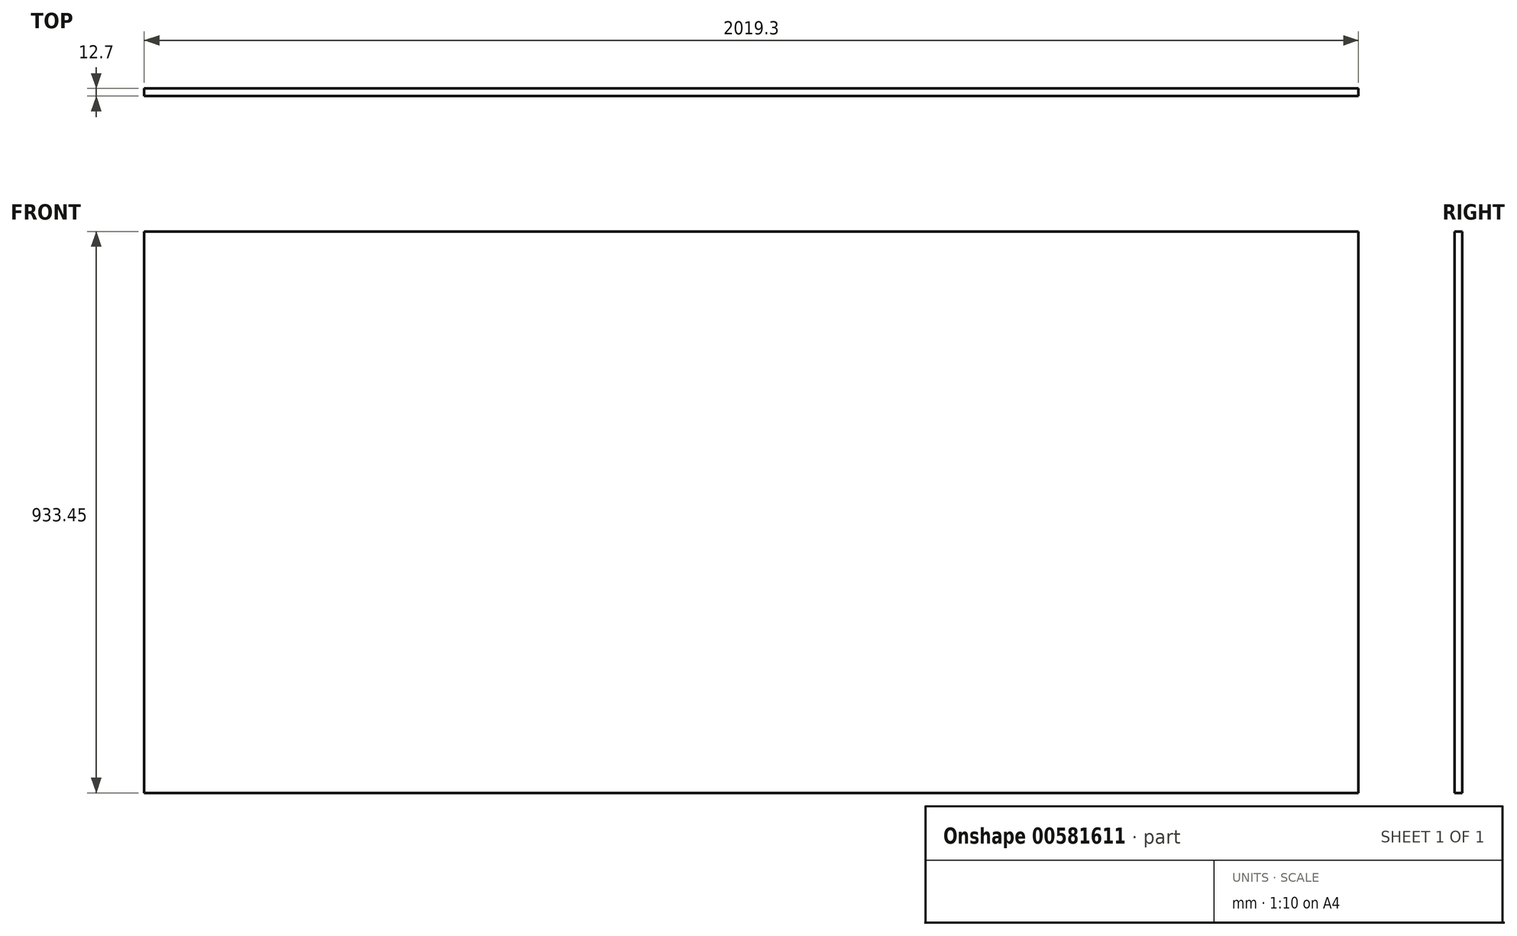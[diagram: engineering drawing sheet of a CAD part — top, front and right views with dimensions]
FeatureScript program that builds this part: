
annotation { "Feature Type Name" : "Feature", "Feature Type Description" : "" }
export const myFeature = defineFeature(function(context is Context, id is Id, definition is map)
    precondition{}
    {
        {
            var Q0;
            Q0=qCreatedBy(makeId("Front.planeOp"),FACE);
            var sketch = newSketch(context, id + "F0", { "sketchPlane" : qUnion([Q0])});
            skLineSegment(sketch, "E0.bottom", {"start": v(-730.71, -474.47) * mm, "end": v(1288.59, -474.47) * mm});
            skLineSegment(sketch, "E0.top", {"start": v(-730.71, 458.98) * mm, "end": v(1288.59, 458.98) * mm});
            skLineSegment(sketch, "E0.left", {"start": v(-730.71, -474.47) * mm, "end": v(-730.71, 458.98) * mm});
            skLineSegment(sketch, "E0.right", {"start": v(1288.59, -474.47) * mm, "end": v(1288.59, 458.98) * mm});
            skSolve(sketch);
        }
        {
            var Q0;
            Q0=makeQuery(id+"F0.imprint","IMPRINT",FACE,{"disambiguationData":[TD([[makeQuery(id+"F0.imprint","IMPRINT",EDGE,{"derivedFrom":sQuery(id+"F0.wireOp",EDGE,"E0.bottom")}),1.0]])]});
            extrude(context, id + "F1", {"entities" : qUnion([Q0]), "depth" : 12.7 * mm, "offsetDistance" : 25.4 * mm});
        }
    });
